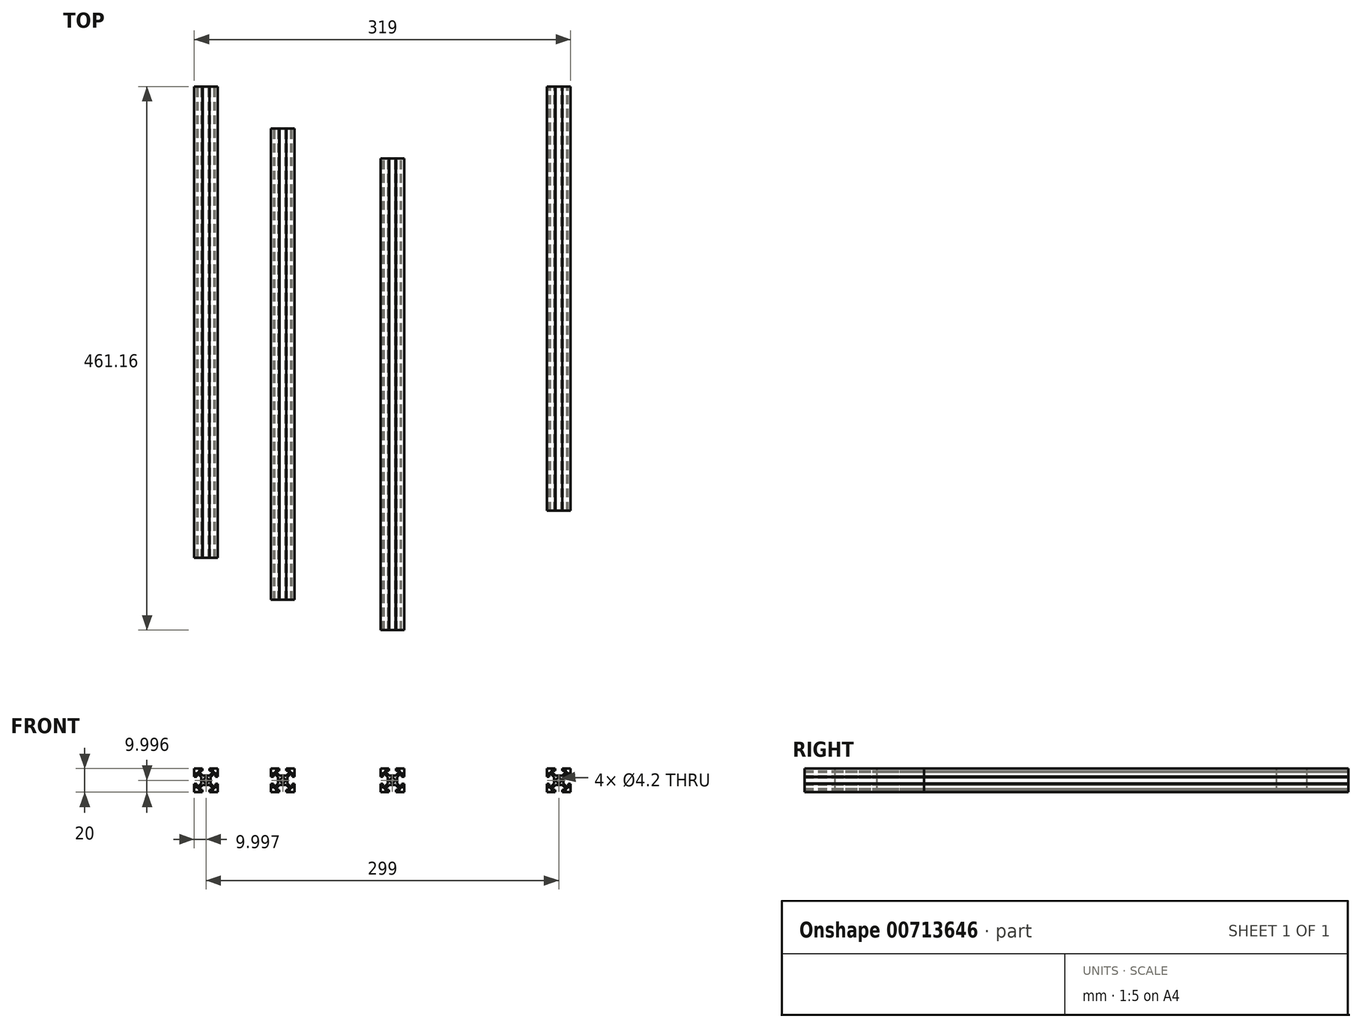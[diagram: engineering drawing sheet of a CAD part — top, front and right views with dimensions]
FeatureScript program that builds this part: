
annotation { "Feature Type Name" : "Feature", "Feature Type Description" : "" }
export const myFeature = defineFeature(function(context is Context, id is Id, definition is map)
    precondition{}
    {
        {
            var Q0;
            Q0=qCreatedBy(makeId("Front.planeOp"),FACE);
            var sketch = newSketch(context, id + "F0", { "sketchPlane" : qUnion([Q0])});
            skLineSegment(sketch, "E0", {"start": v(-3.01, 10) * mm, "end": v(-10.01, 10) * mm});
            skLineSegment(sketch, "E1", {"start": v(-10.01, 10) * mm, "end": v(-10.01, 3) * mm});
            skLineSegment(sketch, "E2", {"start": v(-10.01, 3) * mm, "end": v(-8.01, 3) * mm});
            skLineSegment(sketch, "E3", {"start": v(-8.01, 3) * mm, "end": v(-8.01, 6.75) * mm});
            skLineSegment(sketch, "E4", {"start": v(-8.01, 6.75) * mm, "end": v(-4.01, 2.75) * mm});
            skLineSegment(sketch, "E5", {"start": v(-4.01, 2.75) * mm, "end": v(-4.01, -2.75) * mm});
            skLineSegment(sketch, "E6", {"start": v(-4.01, -2.75) * mm, "end": v(-8.01, -6.75) * mm});
            skLineSegment(sketch, "E7", {"start": v(-8.01, -6.75) * mm, "end": v(-8.01, -3) * mm});
            skLineSegment(sketch, "E8", {"start": v(-8.01, -3) * mm, "end": v(-10.01, -3) * mm});
            skLineSegment(sketch, "E9", {"start": v(-10.01, -3) * mm, "end": v(-10.01, -10) * mm});
            skLineSegment(sketch, "E10", {"start": v(-10.01, -10) * mm, "end": v(-3.01, -10) * mm});
            skLineSegment(sketch, "E11", {"start": v(-3.01, -10) * mm, "end": v(-3.01, -8) * mm});
            skLineSegment(sketch, "E12", {"start": v(-3.01, -8) * mm, "end": v(-6.76, -8) * mm});
            skLineSegment(sketch, "E13", {"start": v(-6.76, -8) * mm, "end": v(-2.76, -4) * mm});
            skLineSegment(sketch, "E14", {"start": v(-2.76, -4) * mm, "end": v(2.86, -4) * mm});
            skLineSegment(sketch, "E15", {"start": v(2.86, -4) * mm, "end": v(6.86, -8) * mm});
            skLineSegment(sketch, "E16", {"start": v(6.86, -8) * mm, "end": v(2.99, -8) * mm});
            skLineSegment(sketch, "E17", {"start": v(2.99, -8) * mm, "end": v(2.99, -10) * mm});
            skLineSegment(sketch, "E18", {"start": v(2.99, -10) * mm, "end": v(9.99, -10) * mm});
            skLineSegment(sketch, "E19", {"start": v(9.99, -10) * mm, "end": v(9.99, -3) * mm});
            skLineSegment(sketch, "E20", {"start": v(9.99, -3) * mm, "end": v(7.99, -3) * mm});
            skLineSegment(sketch, "E21", {"start": v(7.99, -3) * mm, "end": v(7.99, -6.67) * mm});
            skLineSegment(sketch, "E22", {"start": v(7.99, -6.67) * mm, "end": v(3.99, -2.67) * mm});
            skLineSegment(sketch, "E23", {"start": v(3.99, -2.67) * mm, "end": v(3.99, 2.74) * mm});
            skLineSegment(sketch, "E24", {"start": v(3.99, 2.74) * mm, "end": v(7.99, 6.74) * mm});
            skLineSegment(sketch, "E25", {"start": v(7.99, 6.74) * mm, "end": v(7.99, 3) * mm});
            skLineSegment(sketch, "E26", {"start": v(7.99, 3) * mm, "end": v(9.99, 3) * mm});
            skLineSegment(sketch, "E27", {"start": v(9.99, 3) * mm, "end": v(9.99, 10) * mm});
            skLineSegment(sketch, "E28", {"start": v(9.99, 10) * mm, "end": v(2.99, 10) * mm});
            skLineSegment(sketch, "E29", {"start": v(2.99, 10) * mm, "end": v(2.99, 8) * mm});
            skLineSegment(sketch, "E30", {"start": v(2.99, 8) * mm, "end": v(6.86, 8) * mm});
            skLineSegment(sketch, "E31", {"start": v(6.86, 8) * mm, "end": v(2.85, 4) * mm});
            skLineSegment(sketch, "E32", {"start": v(2.85, 4) * mm, "end": v(-2.76, 4) * mm});
            skLineSegment(sketch, "E33", {"start": v(-2.76, 4) * mm, "end": v(-6.76, 8) * mm});
            skLineSegment(sketch, "E34", {"start": v(-6.76, 8) * mm, "end": v(-3.01, 8) * mm});
            skLineSegment(sketch, "E35", {"start": v(-3.01, 8) * mm, "end": v(-3.01, 10) * mm});
            skCircle(sketch, "E36", {"center": v(-0.01, 0) * mm, "radius": 2.1 * mm});
            skSolve(sketch);
        }
        {
            var Q0;
            Q0=makeQuery(id+"F0.imprint","IMPRINT",FACE,{"disambiguationData":[TD([[makeQuery(id+"F0.imprint","IMPRINT",EDGE,{"derivedFrom":sQuery(id+"F0.wireOp",EDGE,"E0")}),1.0]])]});
            extrude(context, id + "F1", {"entities" : qUnion([Q0]), "endBound" : BoundingType.SYMMETRIC, "depth" : 400 * mm});
        }
        {
            var Q0;
            Q0=makeQuery(id+"F1.opExtrude","SWEPT_BODY",BODY,{"disambiguationData":[OSD([sQuery(id+"F0.wireOp",EDGE,"E0"),sQuery(id+"F0.wireOp",EDGE,"E1"),sQuery(id+"F0.wireOp",EDGE,"E2"),sQuery(id+"F0.wireOp",EDGE,"E3"),sQuery(id+"F0.wireOp",EDGE,"E4"),sQuery(id+"F0.wireOp",EDGE,"E5"),sQuery(id+"F0.wireOp",EDGE,"E6"),sQuery(id+"F0.wireOp",EDGE,"E7"),sQuery(id+"F0.wireOp",EDGE,"E8"),sQuery(id+"F0.wireOp",EDGE,"E9"),sQuery(id+"F0.wireOp",EDGE,"E10"),sQuery(id+"F0.wireOp",EDGE,"E11"),sQuery(id+"F0.wireOp",EDGE,"E12"),sQuery(id+"F0.wireOp",EDGE,"E13"),sQuery(id+"F0.wireOp",EDGE,"E14"),sQuery(id+"F0.wireOp",EDGE,"E15"),sQuery(id+"F0.wireOp",EDGE,"E16"),sQuery(id+"F0.wireOp",EDGE,"E17"),sQuery(id+"F0.wireOp",EDGE,"E18"),sQuery(id+"F0.wireOp",EDGE,"E19"),sQuery(id+"F0.wireOp",EDGE,"E20"),sQuery(id+"F0.wireOp",EDGE,"E21"),sQuery(id+"F0.wireOp",EDGE,"E22"),sQuery(id+"F0.wireOp",EDGE,"E23"),sQuery(id+"F0.wireOp",EDGE,"E24"),sQuery(id+"F0.wireOp",EDGE,"E25"),sQuery(id+"F0.wireOp",EDGE,"E26"),sQuery(id+"F0.wireOp",EDGE,"E27"),sQuery(id+"F0.wireOp",EDGE,"E28"),sQuery(id+"F0.wireOp",EDGE,"E29"),sQuery(id+"F0.wireOp",EDGE,"E30"),sQuery(id+"F0.wireOp",EDGE,"E31"),sQuery(id+"F0.wireOp",EDGE,"E32"),sQuery(id+"F0.wireOp",EDGE,"E33"),sQuery(id+"F0.wireOp",EDGE,"E34"),sQuery(id+"F0.wireOp",EDGE,"E35"),sQuery(id+"F0.wireOp",EDGE,"E36")])]});
            transform(context, id + "F2", {"entities" : qUnion([Q0]), "transformType" : TransformType.TRANSLATION_3D, "dx" : 65.08 * mm, "dy" : -35.53 * mm, "dz" : 0 * mm, "makeCopy" : true});
        }
        {
            var Q0;
            Q0=makeQuery(id+"F2.opPattern","COPY",BODY,{"derivedFrom":makeQuery(id+"F1.opExtrude","SWEPT_BODY",BODY,{"disambiguationData":[OSD([sQuery(id+"F0.wireOp",EDGE,"E0"),sQuery(id+"F0.wireOp",EDGE,"E1"),sQuery(id+"F0.wireOp",EDGE,"E2"),sQuery(id+"F0.wireOp",EDGE,"E3"),sQuery(id+"F0.wireOp",EDGE,"E4"),sQuery(id+"F0.wireOp",EDGE,"E5"),sQuery(id+"F0.wireOp",EDGE,"E6"),sQuery(id+"F0.wireOp",EDGE,"E7"),sQuery(id+"F0.wireOp",EDGE,"E8"),sQuery(id+"F0.wireOp",EDGE,"E9"),sQuery(id+"F0.wireOp",EDGE,"E10"),sQuery(id+"F0.wireOp",EDGE,"E11"),sQuery(id+"F0.wireOp",EDGE,"E12"),sQuery(id+"F0.wireOp",EDGE,"E13"),sQuery(id+"F0.wireOp",EDGE,"E14"),sQuery(id+"F0.wireOp",EDGE,"E15"),sQuery(id+"F0.wireOp",EDGE,"E16"),sQuery(id+"F0.wireOp",EDGE,"E17"),sQuery(id+"F0.wireOp",EDGE,"E18"),sQuery(id+"F0.wireOp",EDGE,"E19"),sQuery(id+"F0.wireOp",EDGE,"E20"),sQuery(id+"F0.wireOp",EDGE,"E21"),sQuery(id+"F0.wireOp",EDGE,"E22"),sQuery(id+"F0.wireOp",EDGE,"E23"),sQuery(id+"F0.wireOp",EDGE,"E24"),sQuery(id+"F0.wireOp",EDGE,"E25"),sQuery(id+"F0.wireOp",EDGE,"E26"),sQuery(id+"F0.wireOp",EDGE,"E27"),sQuery(id+"F0.wireOp",EDGE,"E28"),sQuery(id+"F0.wireOp",EDGE,"E29"),sQuery(id+"F0.wireOp",EDGE,"E30"),sQuery(id+"F0.wireOp",EDGE,"E31"),sQuery(id+"F0.wireOp",EDGE,"E32"),sQuery(id+"F0.wireOp",EDGE,"E33"),sQuery(id+"F0.wireOp",EDGE,"E34"),sQuery(id+"F0.wireOp",EDGE,"E35"),sQuery(id+"F0.wireOp",EDGE,"E36")])]}),"instanceName":"1"});
            transform(context, id + "F3", {"entities" : qUnion([Q0]), "transformType" : TransformType.TRANSLATION_3D, "dx" : 92.84 * mm, "dy" : -25.64 * mm, "dz" : 0 * mm, "makeCopy" : true});
        }
        {
            var Q0;
            Q0=makeQuery(id+"F1.opExtrude","SWEPT_BODY",BODY,{"disambiguationData":[OSD([sQuery(id+"F0.wireOp",EDGE,"E0"),sQuery(id+"F0.wireOp",EDGE,"E1"),sQuery(id+"F0.wireOp",EDGE,"E2"),sQuery(id+"F0.wireOp",EDGE,"E3"),sQuery(id+"F0.wireOp",EDGE,"E4"),sQuery(id+"F0.wireOp",EDGE,"E5"),sQuery(id+"F0.wireOp",EDGE,"E6"),sQuery(id+"F0.wireOp",EDGE,"E7"),sQuery(id+"F0.wireOp",EDGE,"E8"),sQuery(id+"F0.wireOp",EDGE,"E9"),sQuery(id+"F0.wireOp",EDGE,"E10"),sQuery(id+"F0.wireOp",EDGE,"E11"),sQuery(id+"F0.wireOp",EDGE,"E12"),sQuery(id+"F0.wireOp",EDGE,"E13"),sQuery(id+"F0.wireOp",EDGE,"E14"),sQuery(id+"F0.wireOp",EDGE,"E15"),sQuery(id+"F0.wireOp",EDGE,"E16"),sQuery(id+"F0.wireOp",EDGE,"E17"),sQuery(id+"F0.wireOp",EDGE,"E18"),sQuery(id+"F0.wireOp",EDGE,"E19"),sQuery(id+"F0.wireOp",EDGE,"E20"),sQuery(id+"F0.wireOp",EDGE,"E21"),sQuery(id+"F0.wireOp",EDGE,"E22"),sQuery(id+"F0.wireOp",EDGE,"E23"),sQuery(id+"F0.wireOp",EDGE,"E24"),sQuery(id+"F0.wireOp",EDGE,"E25"),sQuery(id+"F0.wireOp",EDGE,"E26"),sQuery(id+"F0.wireOp",EDGE,"E27"),sQuery(id+"F0.wireOp",EDGE,"E28"),sQuery(id+"F0.wireOp",EDGE,"E29"),sQuery(id+"F0.wireOp",EDGE,"E30"),sQuery(id+"F0.wireOp",EDGE,"E31"),sQuery(id+"F0.wireOp",EDGE,"E32"),sQuery(id+"F0.wireOp",EDGE,"E33"),sQuery(id+"F0.wireOp",EDGE,"E34"),sQuery(id+"F0.wireOp",EDGE,"E35"),sQuery(id+"F0.wireOp",EDGE,"E36")])]});
            transform(context, id + "F4", {"entities" : qUnion([Q0]), "transformType" : TransformType.TRANSLATION_3D, "dx" : 299 * mm, "dy" : 0 * mm, "dz" : 0 * mm, "makeCopy" : true});
        }
        {
            var Q0;
            Q0=makeQuery(id+"F4.opPattern","COPY",FACE,{"derivedFrom":makeQuery(id+"F1.opExtrude","CAP_FACE",FACE,{"disambiguationData":[OSD([sQuery(id+"F0.wireOp",EDGE,"E0"),sQuery(id+"F0.wireOp",EDGE,"E1"),sQuery(id+"F0.wireOp",EDGE,"E2"),sQuery(id+"F0.wireOp",EDGE,"E3"),sQuery(id+"F0.wireOp",EDGE,"E4"),sQuery(id+"F0.wireOp",EDGE,"E5"),sQuery(id+"F0.wireOp",EDGE,"E6"),sQuery(id+"F0.wireOp",EDGE,"E7"),sQuery(id+"F0.wireOp",EDGE,"E8"),sQuery(id+"F0.wireOp",EDGE,"E9"),sQuery(id+"F0.wireOp",EDGE,"E10"),sQuery(id+"F0.wireOp",EDGE,"E11"),sQuery(id+"F0.wireOp",EDGE,"E12"),sQuery(id+"F0.wireOp",EDGE,"E13"),sQuery(id+"F0.wireOp",EDGE,"E14"),sQuery(id+"F0.wireOp",EDGE,"E15"),sQuery(id+"F0.wireOp",EDGE,"E16"),sQuery(id+"F0.wireOp",EDGE,"E17"),sQuery(id+"F0.wireOp",EDGE,"E18"),sQuery(id+"F0.wireOp",EDGE,"E19"),sQuery(id+"F0.wireOp",EDGE,"E20"),sQuery(id+"F0.wireOp",EDGE,"E21"),sQuery(id+"F0.wireOp",EDGE,"E22"),sQuery(id+"F0.wireOp",EDGE,"E23"),sQuery(id+"F0.wireOp",EDGE,"E24"),sQuery(id+"F0.wireOp",EDGE,"E25"),sQuery(id+"F0.wireOp",EDGE,"E26"),sQuery(id+"F0.wireOp",EDGE,"E27"),sQuery(id+"F0.wireOp",EDGE,"E28"),sQuery(id+"F0.wireOp",EDGE,"E29"),sQuery(id+"F0.wireOp",EDGE,"E30"),sQuery(id+"F0.wireOp",EDGE,"E31"),sQuery(id+"F0.wireOp",EDGE,"E32"),sQuery(id+"F0.wireOp",EDGE,"E33"),sQuery(id+"F0.wireOp",EDGE,"E34"),sQuery(id+"F0.wireOp",EDGE,"E35"),sQuery(id+"F0.wireOp",EDGE,"E36")])],"isStart":false}),"instanceName":"1"});
            extrude(context, id + "F5", {"entities" : qUnion([Q0]), "operationType" : NewBodyOperationType.REMOVE, "oppositeDirection" : true, "depth" : 40 * mm});
        }
    });
